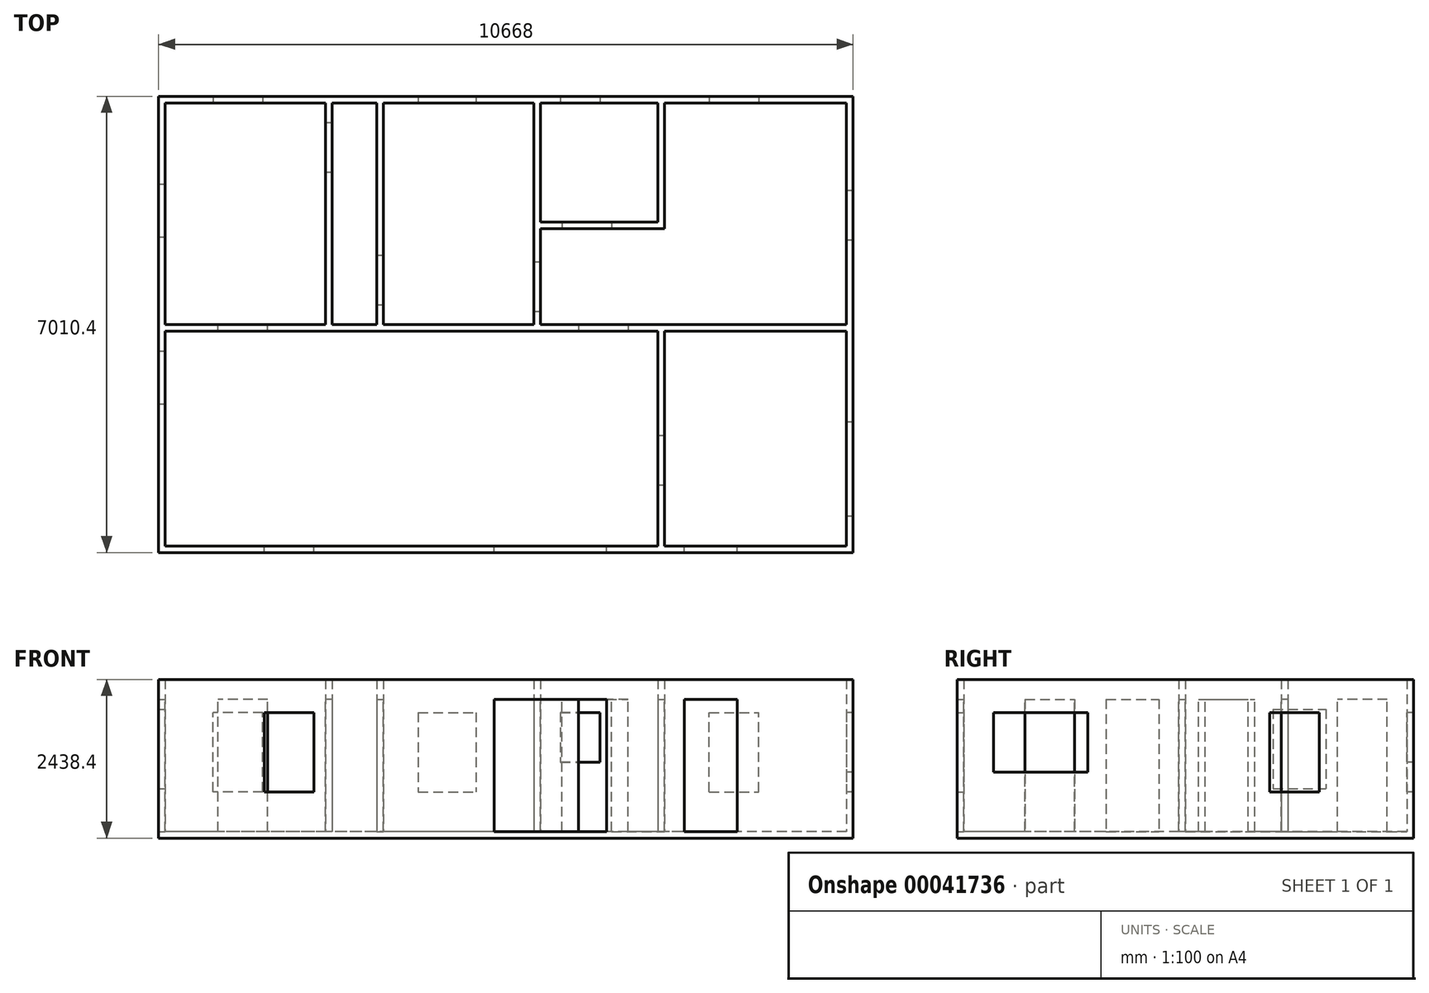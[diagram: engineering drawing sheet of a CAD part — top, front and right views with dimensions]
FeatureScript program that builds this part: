
annotation { "Feature Type Name" : "Feature", "Feature Type Description" : "" }
export const myFeature = defineFeature(function(context is Context, id is Id, definition is map)
    precondition{}
    {
        {
            var Q0;
            Q0=qCreatedBy(makeId("Top.planeOp"),FACE);
            var sketch = newSketch(context, id + "F34", { "sketchPlane" : qUnion([Q0])});
            skLineSegment(sketch, "E0.bottom", {"start": v(10668, 7010.4) * mm, "end": v(0, 7010.4) * mm});
            skLineSegment(sketch, "E0.top", {"start": v(10668, 0) * mm, "end": v(0, 0) * mm});
            skLineSegment(sketch, "E0.left", {"start": v(10668, 7010.4) * mm, "end": v(10668, 0) * mm});
            skLineSegment(sketch, "E0.right", {"start": v(0, 7010.4) * mm, "end": v(0, 0) * mm});
            skSolve(sketch);
        }
        {
            var Q0;
            Q0=qSketchRegion(id+"F34",true);
            extrude(context, id + "F0", {"entities" : qUnion([Q0]), "depth" : 2438.4 * mm});
        }
        {
            var Q0;
            Q0=makeQuery(id+"F0.opExtrude","CAP_FACE",FACE,{"disambiguationData":[OSD([sQuery(id+"F34.wireOp",EDGE,"E0.bottom"),sQuery(id+"F34.wireOp",EDGE,"E0.top"),sQuery(id+"F34.wireOp",EDGE,"E0.left"),sQuery(id+"F34.wireOp",EDGE,"E0.right")])],"isStart":false});
            shell(context, id + "F35", {"entities" : qUnion([Q0]), "thickness" : 101.6 * mm});
        }
        {
            var Q0;
            Q0=makeQuery(id+"F35.opShell","OFFSET_FACE",FACE,{"disambiguationData":[OSD([sQuery(id+"F34.wireOp",EDGE,"E0.bottom"),sQuery(id+"F34.wireOp",EDGE,"E0.top"),sQuery(id+"F34.wireOp",EDGE,"E0.left"),sQuery(id+"F34.wireOp",EDGE,"E0.right")])]});
            var sketch = newSketch(context, id + "F1", { "sketchPlane" : qUnion([Q0])});
            skLineSegment(sketch, "E1", {"start": v(10566.4, 3403.6) * mm, "end": v(101.6, 3403.6) * mm});
            skLineSegment(sketch, "E2.1", {"start": v(10566.4, 3505.2) * mm, "end": v(101.6, 3505.2) * mm});
            skLineSegment(sketch, "E3", {"start": v(3454.4, 6908.8) * mm, "end": v(3454.4, 3505.2) * mm});
            skLineSegment(sketch, "E4", {"start": v(5867.4, 6908.8) * mm, "end": v(5867.4, 3505.2) * mm});
            skLineSegment(sketch, "E5.0", {"start": v(3352.8, 6908.8) * mm, "end": v(3352.8, 3505.2) * mm});
            skLineSegment(sketch, "E6.0", {"start": v(5765.8, 6908.8) * mm, "end": v(5765.8, 3505.2) * mm});
            skLineSegment(sketch, "E7.bottom", {"start": v(2565.4, 3505.2) * mm, "end": v(2667, 3505.2) * mm});
            skLineSegment(sketch, "E7.top", {"start": v(2565.4, 6908.8) * mm, "end": v(2667, 6908.8) * mm});
            skLineSegment(sketch, "E7.left", {"start": v(2565.4, 3505.2) * mm, "end": v(2565.4, 6908.8) * mm});
            skLineSegment(sketch, "E7.right", {"start": v(2667, 3505.2) * mm, "end": v(2667, 6908.8) * mm});
            skLineSegment(sketch, "E8", {"start": v(7670.8, 6908.8) * mm, "end": v(7670.8, 5080) * mm});
            skLineSegment(sketch, "E9", {"start": v(7670.8, 5080) * mm, "end": v(5867.4, 5080) * mm});
            skLineSegment(sketch, "E10", {"start": v(5867.4, 4978.4) * mm, "end": v(7772.4, 4978.4) * mm});
            skLineSegment(sketch, "E11", {"start": v(7772.4, 4978.4) * mm, "end": v(7772.4, 6908.8) * mm});
            skLineSegment(sketch, "E12", {"start": v(7670.8, 3403.6) * mm, "end": v(7670.8, 101.6) * mm});
            skLineSegment(sketch, "E13", {"start": v(7772.4, 3403.6) * mm, "end": v(7772.4, 101.6) * mm});
            skSolve(sketch);
        }
        {
            var Q0;
            Q0=qSketchRegion(id+"F1",true);
            var Q1;
            {var subQ4=sQuery(id+"F1.wireOp",EDGE,"E1");Q1=makeQuery(id+"F1.imprint","IMPRINT",FACE,{"disambiguationData":[TD([[makeQuery(id+"F1.imprint","IMPRINT",EDGE,{"derivedFrom":subQ4}),-1.0]])]});}
            var Q2;
            {var subQ0=sQuery(id+"F1.wireOp",EDGE,"E3");Q2=makeQuery(id+"F1.imprint","IMPRINT",FACE,{"disambiguationData":[TD([[makeQuery(id+"F1.imprint","IMPRINT",EDGE,{"derivedFrom":subQ0}),-1.0]])]});}
            var Q3;
            {var subQ0=sQuery(id+"F1.wireOp",EDGE,"E4");Q3=makeQuery(id+"F1.imprint","IMPRINT",FACE,{"disambiguationData":[TD([[makeQuery(id+"F1.imprint","IMPRINT",EDGE,{"derivedFrom":subQ0}),-1.0]])]});}
            var Q4;
            {var subQ2=sQuery(id+"F1.wireOp",EDGE,"E8");Q4=makeQuery(id+"F1.imprint","IMPRINT",FACE,{"disambiguationData":[TD([[makeQuery(id+"F1.imprint","IMPRINT",EDGE,{"derivedFrom":subQ2}),1.0]])]});}
            var Q5;
            {var subQ0=sQuery(id+"F1.wireOp",EDGE,"E12");Q5=makeQuery(id+"F1.imprint","IMPRINT",FACE,{"disambiguationData":[TD([[makeQuery(id+"F1.imprint","IMPRINT",EDGE,{"derivedFrom":subQ0}),1.0]])]});}
            var Q6;
            Q6=makeQuery(id+"F0.opExtrude","CAP_FACE",FACE,{"disambiguationData":[OSD([sQuery(id+"F34.wireOp",EDGE,"E0.bottom"),sQuery(id+"F34.wireOp",EDGE,"E0.top"),sQuery(id+"F34.wireOp",EDGE,"E0.left"),sQuery(id+"F34.wireOp",EDGE,"E0.right")])],"isStart":false});
            extrude(context, id + "F2", {"entities" : qUnion([Q0, Q1, Q2, Q3, Q4, Q5]), "operationType" : NewBodyOperationType.ADD, "endBound" : BoundingType.UP_TO_SURFACE, "endBoundEntityFace" : qUnion([Q6]), "depth" : 30.48 * mm});
        }
        {
            var Q0;
            {var subQ0=sQuery(id+"F1.wireOp",EDGE,"E2.1");Q0=makeQuery(id+"F2.opExtrude","SWEPT_FACE",FACE,{"disambiguationData":[OSD([subQ0]),TDD([makeQuery(id+"F1.imprint","IMPRINT",EDGE,{"disambiguationData":[TD([[makeQuery(id+"F1.imprint","INTERSECT",VERTEX,{"derivedFrom":[subQ0,sQuery(id+"F1.wireOp",EDGE,"E5.0")]}),-1.0]])],"derivedFrom":subQ0})])]});}
            var sketch = newSketch(context, id + "F36", { "sketchPlane" : qUnion([Q0])});
            skLineSegment(sketch, "E14.bottom", {"start": v(-1676.4, 101.6) * mm, "end": v(-914.4, 101.6) * mm});
            skLineSegment(sketch, "E14.top", {"start": v(-1676.4, 2133.6) * mm, "end": v(-914.4, 2133.6) * mm});
            skLineSegment(sketch, "E14.left", {"start": v(-1676.4, 101.6) * mm, "end": v(-1676.4, 2133.6) * mm});
            skLineSegment(sketch, "E14.right", {"start": v(-914.4, 101.6) * mm, "end": v(-914.4, 2133.6) * mm});
            skSolve(sketch);
        }
        {
            var Q0;
            Q0=qSketchRegion(id+"F36",true);
            extrude(context, id + "F3", {"entities" : qUnion([Q0]), "operationType" : NewBodyOperationType.REMOVE, "endBound" : BoundingType.UP_TO_NEXT, "oppositeDirection" : true, "depth" : 30.48 * mm});
        }
        {
            var Q0;
            Q0=makeQuery(id+"F35.opShell","OFFSET_FACE",FACE,{"disambiguationData":[OSD([sQuery(id+"F34.wireOp",EDGE,"E0.top")])]});
            var sketch = newSketch(context, id + "F37", { "sketchPlane" : qUnion([Q0])});
            skLineSegment(sketch, "E15.bottom", {"start": v(-8890, 101.6) * mm, "end": v(-8077.2, 101.6) * mm});
            skLineSegment(sketch, "E15.top", {"start": v(-8890, 2133.6) * mm, "end": v(-8077.2, 2133.6) * mm});
            skLineSegment(sketch, "E15.left", {"start": v(-8890, 101.6) * mm, "end": v(-8890, 2133.6) * mm});
            skLineSegment(sketch, "E15.right", {"start": v(-8077.2, 101.6) * mm, "end": v(-8077.2, 2133.6) * mm});
            skSolve(sketch);
        }
        {
            var Q0;
            Q0=qSketchRegion(id+"F37",true);
            extrude(context, id + "F38", {"entities" : qUnion([Q0]), "operationType" : NewBodyOperationType.REMOVE, "endBound" : BoundingType.UP_TO_NEXT, "oppositeDirection" : true, "depth" : 30.48 * mm});
        }
        {
            var Q0;
            {var subQ0=sQuery(id+"F34.wireOp",EDGE,"E0.right");var subQ2=sQuery(id+"F34.wireOp",EDGE,"E0.top");Q0=makeQuery(id+"F2.boolean.opBoolean","SPLIT",FACE,{"disambiguationData":[TD([makeQuery(id+"F35.opShell","OFFSET_FACE",FACE,{"disambiguationData":[OSD([subQ2])]})])],"derivedFrom":makeQuery(id+"F35.opShell","OFFSET_FACE",FACE,{"disambiguationData":[OSD([subQ0])]})});}
            var sketch = newSketch(context, id + "F39", { "sketchPlane" : qUnion([Q0])});
            skLineSegment(sketch, "E16.bottom", {"start": v(3098.8, 101.6) * mm, "end": v(2286, 101.6) * mm});
            skLineSegment(sketch, "E16.top", {"start": v(3098.8, 2133.6) * mm, "end": v(2286, 2133.6) * mm});
            skLineSegment(sketch, "E16.left", {"start": v(3098.8, 101.6) * mm, "end": v(3098.8, 2133.6) * mm});
            skLineSegment(sketch, "E16.right", {"start": v(2286, 101.6) * mm, "end": v(2286, 2133.6) * mm});
            skSolve(sketch);
        }
        {
            var Q0;
            Q0=qSketchRegion(id+"F39",true);
            extrude(context, id + "F4", {"entities" : qUnion([Q0]), "operationType" : NewBodyOperationType.REMOVE, "endBound" : BoundingType.UP_TO_NEXT, "oppositeDirection" : true, "depth" : 30.48 * mm});
        }
        {
            var Q0;
            {var subQ0=sQuery(id+"F34.wireOp",EDGE,"E0.right");var subQ3=sQuery(id+"F34.wireOp",EDGE,"E0.bottom");Q0=makeQuery(id+"F2.boolean.opBoolean","SPLIT",FACE,{"disambiguationData":[TD([makeQuery(id+"F35.opShell","OFFSET_FACE",FACE,{"disambiguationData":[OSD([subQ3])]})])],"derivedFrom":makeQuery(id+"F35.opShell","OFFSET_FACE",FACE,{"disambiguationData":[OSD([subQ0])]})});}
            var sketch = newSketch(context, id + "F5", { "sketchPlane" : qUnion([Q0])});
            skLineSegment(sketch, "E17.bottom", {"start": v(4851.4, 1981.2) * mm, "end": v(5664.2, 1981.2) * mm});
            skLineSegment(sketch, "E17.top", {"start": v(4851.4, 762) * mm, "end": v(5664.2, 762) * mm});
            skLineSegment(sketch, "E17.left", {"start": v(4851.4, 1981.2) * mm, "end": v(4851.4, 762) * mm});
            skLineSegment(sketch, "E17.right", {"start": v(5664.2, 1981.2) * mm, "end": v(5664.2, 762) * mm});
            skSolve(sketch);
        }
        {
            var Q0;
            Q0 = qSketchRegion(id + "F5", true);
            extrude(context, id + "F6", {"entities" : qUnion([Q0]), "operationType" : NewBodyOperationType.REMOVE, "endBound" : BoundingType.UP_TO_NEXT, "oppositeDirection" : true, "depth" : 30.48 * mm});
        }
        {
            var Q0;
            Q0=makeQuery(id+"F35.opShell","OFFSET_FACE",FACE,{"disambiguationData":[OSD([sQuery(id+"F34.wireOp",EDGE,"E0.bottom")])]});
            var sketch = newSketch(context, id + "F7", { "sketchPlane" : qUnion([Q0])});
            skLineSegment(sketch, "E18.bottom", {"start": v(838.2, 1930.4) * mm, "end": v(1600.2, 1930.4) * mm});
            skLineSegment(sketch, "E18.top", {"start": v(838.2, 711.2) * mm, "end": v(1600.2, 711.2) * mm});
            skLineSegment(sketch, "E18.left", {"start": v(838.2, 1930.4) * mm, "end": v(838.2, 711.2) * mm});
            skLineSegment(sketch, "E18.right", {"start": v(1600.2, 1930.4) * mm, "end": v(1600.2, 711.2) * mm});
            skSolve(sketch);
        }
        {
            var Q0;
            Q0 = qSketchRegion(id + "F7", true);
            extrude(context, id + "F40", {"entities" : qUnion([Q0]), "operationType" : NewBodyOperationType.REMOVE, "endBound" : BoundingType.UP_TO_NEXT, "oppositeDirection" : true, "depth" : 30.48 * mm});
        }
        {
            var Q0;
            Q0=makeQuery(id+"F2.opExtrude","SWEPT_FACE",FACE,{"disambiguationData":[OSD([sQuery(id+"F1.wireOp",EDGE,"E13")])]});
            var sketch = newSketch(context, id + "F8", { "sketchPlane" : qUnion([Q0])});
            skLineSegment(sketch, "E19.bottom", {"start": v(1041.4, 101.6) * mm, "end": v(1803.4, 101.6) * mm});
            skLineSegment(sketch, "E19.top", {"start": v(1041.4, 2133.6) * mm, "end": v(1803.4, 2133.6) * mm});
            skLineSegment(sketch, "E19.left", {"start": v(1041.4, 101.6) * mm, "end": v(1041.4, 2133.6) * mm});
            skLineSegment(sketch, "E19.right", {"start": v(1803.4, 101.6) * mm, "end": v(1803.4, 2133.6) * mm});
            skSolve(sketch);
        }
        {
            var Q0;
            Q0 = qSketchRegion(id + "F8", true);
            extrude(context, id + "F9", {"entities" : qUnion([Q0]), "operationType" : NewBodyOperationType.REMOVE, "endBound" : BoundingType.UP_TO_NEXT, "oppositeDirection" : true, "depth" : 30.48 * mm});
        }
        {
            var Q0;
            {var subQ0=sQuery(id+"F1.wireOp",EDGE,"E1");Q0=makeQuery(id+"F2.opExtrude","SWEPT_FACE",FACE,{"disambiguationData":[OSD([subQ0]),TDD([makeQuery(id+"F1.imprint","IMPRINT",EDGE,{"disambiguationData":[TD([[makeQuery(id+"F1.imprint","INTERSECT",VERTEX,{"derivedFrom":[subQ0,sQuery(id+"F1.wireOp",EDGE,"E12")]}),-1.0]])],"derivedFrom":subQ0})])]});}
            var sketch = newSketch(context, id + "F10", { "sketchPlane" : qUnion([Q0])});
            skLineSegment(sketch, "E20.bottom", {"start": v(6451.6, 101.6) * mm, "end": v(7213.6, 101.6) * mm});
            skLineSegment(sketch, "E20.top", {"start": v(6451.6, 2133.6) * mm, "end": v(7213.6, 2133.6) * mm});
            skLineSegment(sketch, "E20.left", {"start": v(6451.6, 101.6) * mm, "end": v(6451.6, 2133.6) * mm});
            skLineSegment(sketch, "E20.right", {"start": v(7213.6, 101.6) * mm, "end": v(7213.6, 2133.6) * mm});
            skSolve(sketch);
        }
        {
            var Q0;
            Q0 = qSketchRegion(id + "F10", true);
            extrude(context, id + "F11", {"entities" : qUnion([Q0]), "operationType" : NewBodyOperationType.REMOVE, "endBound" : BoundingType.UP_TO_NEXT, "oppositeDirection" : true, "depth" : 30.48 * mm});
        }
        {
            var Q0;
            Q0=makeQuery(id+"F2.opExtrude","SWEPT_FACE",FACE,{"disambiguationData":[OSD([sQuery(id+"F1.wireOp",EDGE,"E10")])]});
            var sketch = newSketch(context, id + "F12", { "sketchPlane" : qUnion([Q0])});
            skLineSegment(sketch, "E21.bottom", {"start": v(6197.6, 101.6) * mm, "end": v(6959.6, 101.6) * mm});
            skLineSegment(sketch, "E21.top", {"start": v(6197.6, 2133.6) * mm, "end": v(6959.6, 2133.6) * mm});
            skLineSegment(sketch, "E21.left", {"start": v(6197.6, 101.6) * mm, "end": v(6197.6, 2133.6) * mm});
            skLineSegment(sketch, "E21.right", {"start": v(6959.6, 101.6) * mm, "end": v(6959.6, 2133.6) * mm});
            skSolve(sketch);
        }
        {
            var Q0;
            Q0 = qSketchRegion(id + "F12", true);
            extrude(context, id + "F13", {"entities" : qUnion([Q0]), "operationType" : NewBodyOperationType.REMOVE, "endBound" : BoundingType.UP_TO_NEXT, "oppositeDirection" : true, "depth" : 30.48 * mm});
        }
        {
            var Q0;
            {var subQ0=sQuery(id+"F1.wireOp",EDGE,"E4");Q0=makeQuery(id+"F2.opExtrude","SWEPT_FACE",FACE,{"disambiguationData":[OSD([subQ0]),TDD([makeQuery(id+"F1.imprint","IMPRINT",EDGE,{"disambiguationData":[TD([[makeQuery(id+"F1.imprint","INTERSECT",VERTEX,{"derivedFrom":[sQuery(id+"F1.wireOp",EDGE,"E2.1"),subQ0]}),1.0]])],"derivedFrom":subQ0})])]});}
            var sketch = newSketch(context, id + "F14", { "sketchPlane" : qUnion([Q0])});
            skLineSegment(sketch, "E22.bottom", {"start": v(3708.4, 101.6) * mm, "end": v(4470.4, 101.6) * mm});
            skLineSegment(sketch, "E22.top", {"start": v(3708.4, 2133.6) * mm, "end": v(4470.4, 2133.6) * mm});
            skLineSegment(sketch, "E22.left", {"start": v(3708.4, 101.6) * mm, "end": v(3708.4, 2133.6) * mm});
            skLineSegment(sketch, "E22.right", {"start": v(4470.4, 101.6) * mm, "end": v(4470.4, 2133.6) * mm});
            skSolve(sketch);
        }
        {
            var Q0;
            Q0 = qSketchRegion(id + "F14", true);
            extrude(context, id + "F15", {"entities" : qUnion([Q0]), "operationType" : NewBodyOperationType.REMOVE, "endBound" : BoundingType.UP_TO_NEXT, "oppositeDirection" : true, "depth" : 30.48 * mm});
        }
        {
            var Q0;
            {var subQ3=sQuery(id+"F34.wireOp",EDGE,"E0.bottom");Q0=makeQuery(id+"F2.boolean.opBoolean","SPLIT",FACE,{"disambiguationData":[TD([makeQuery(id+"F2.opExtrude","SWEPT_FACE",FACE,{"disambiguationData":[OSD([sQuery(id+"F1.wireOp",EDGE,"E3")])]})])],"derivedFrom":makeQuery(id+"F35.opShell","OFFSET_FACE",FACE,{"disambiguationData":[OSD([subQ3])]})});}
            var sketch = newSketch(context, id + "F16", { "sketchPlane" : qUnion([Q0])});
            skLineSegment(sketch, "E23.bottom", {"start": v(3987.8, 1930.4) * mm, "end": v(4876.8, 1930.4) * mm});
            skLineSegment(sketch, "E23.top", {"start": v(3987.8, 711.2) * mm, "end": v(4876.8, 711.2) * mm});
            skLineSegment(sketch, "E23.left", {"start": v(3987.8, 1930.4) * mm, "end": v(3987.8, 711.2) * mm});
            skLineSegment(sketch, "E23.right", {"start": v(4876.8, 1930.4) * mm, "end": v(4876.8, 711.2) * mm});
            skSolve(sketch);
        }
        {
            var Q0;
            Q0 = qSketchRegion(id + "F16", true);
            extrude(context, id + "F17", {"entities" : qUnion([Q0]), "operationType" : NewBodyOperationType.REMOVE, "endBound" : BoundingType.UP_TO_NEXT, "oppositeDirection" : true, "depth" : 30.48 * mm});
        }
        {
            var Q0;
            {var subQ3=sQuery(id+"F34.wireOp",EDGE,"E0.bottom");Q0=makeQuery(id+"F2.boolean.opBoolean","SPLIT",FACE,{"disambiguationData":[TD([makeQuery(id+"F2.opExtrude","SWEPT_FACE",FACE,{"disambiguationData":[OSD([sQuery(id+"F1.wireOp",EDGE,"E8")])]})])],"derivedFrom":makeQuery(id+"F35.opShell","OFFSET_FACE",FACE,{"disambiguationData":[OSD([subQ3])]})});}
            var sketch = newSketch(context, id + "F18", { "sketchPlane" : qUnion([Q0])});
            skLineSegment(sketch, "E24.bottom", {"start": v(6172.2, 1930.4) * mm, "end": v(6781.8, 1930.4) * mm});
            skLineSegment(sketch, "E24.top", {"start": v(6172.2, 1168.4) * mm, "end": v(6781.8, 1168.4) * mm});
            skLineSegment(sketch, "E24.left", {"start": v(6172.2, 1930.4) * mm, "end": v(6172.2, 1168.4) * mm});
            skLineSegment(sketch, "E24.right", {"start": v(6781.8, 1930.4) * mm, "end": v(6781.8, 1168.4) * mm});
            skSolve(sketch);
        }
        {
            var Q0;
            Q0 = qSketchRegion(id + "F18", true);
            extrude(context, id + "F19", {"entities" : qUnion([Q0]), "operationType" : NewBodyOperationType.REMOVE, "endBound" : BoundingType.UP_TO_NEXT, "oppositeDirection" : true, "depth" : 30.48 * mm});
        }
        {
            var Q0;
            {var subQ1=sQuery(id+"F34.wireOp",EDGE,"E0.left");var subQ2=sQuery(id+"F34.wireOp",EDGE,"E0.top");Q0=makeQuery(id+"F2.boolean.opBoolean","SPLIT",FACE,{"disambiguationData":[TD([makeQuery(id+"F35.opShell","OFFSET_FACE",FACE,{"disambiguationData":[OSD([subQ2])]})])],"derivedFrom":makeQuery(id+"F35.opShell","OFFSET_FACE",FACE,{"disambiguationData":[OSD([subQ1])]})});}
            var sketch = newSketch(context, id + "F20", { "sketchPlane" : qUnion([Q0])});
            skLineSegment(sketch, "E25.bottom", {"start": v(-558.8, 1930.4) * mm, "end": v(-2006.6, 1930.4) * mm});
            skLineSegment(sketch, "E25.top", {"start": v(-558.8, 1016) * mm, "end": v(-2006.6, 1016) * mm});
            skLineSegment(sketch, "E25.left", {"start": v(-558.8, 1930.4) * mm, "end": v(-558.8, 1016) * mm});
            skLineSegment(sketch, "E25.right", {"start": v(-2006.6, 1930.4) * mm, "end": v(-2006.6, 1016) * mm});
            skSolve(sketch);
        }
        {
            var Q0;
            Q0 = qSketchRegion(id + "F20", true);
            extrude(context, id + "F21", {"entities" : qUnion([Q0]), "operationType" : NewBodyOperationType.REMOVE, "endBound" : BoundingType.UP_TO_NEXT, "oppositeDirection" : true, "depth" : 30.48 * mm});
        }
        {
            var Q0;
            {var subQ1=sQuery(id+"F34.wireOp",EDGE,"E0.left");var subQ3=sQuery(id+"F34.wireOp",EDGE,"E0.bottom");Q0=makeQuery(id+"F2.boolean.opBoolean","SPLIT",FACE,{"disambiguationData":[TD([makeQuery(id+"F35.opShell","OFFSET_FACE",FACE,{"disambiguationData":[OSD([subQ1])]})])],"derivedFrom":makeQuery(id+"F35.opShell","OFFSET_FACE",FACE,{"disambiguationData":[OSD([subQ3])]})});}
            var sketch = newSketch(context, id + "F22", { "sketchPlane" : qUnion([Q0])});
            skLineSegment(sketch, "E26.bottom", {"start": v(8458.2, 711.2) * mm, "end": v(9220.2, 711.2) * mm});
            skLineSegment(sketch, "E26.top", {"start": v(8458.2, 1930.4) * mm, "end": v(9220.2, 1930.4) * mm});
            skLineSegment(sketch, "E26.left", {"start": v(8458.2, 711.2) * mm, "end": v(8458.2, 1930.4) * mm});
            skLineSegment(sketch, "E26.right", {"start": v(9220.2, 711.2) * mm, "end": v(9220.2, 1930.4) * mm});
            skSolve(sketch);
        }
        {
            var Q0;
            Q0 = qSketchRegion(id + "F22", true);
            extrude(context, id + "F23", {"entities" : qUnion([Q0]), "operationType" : NewBodyOperationType.REMOVE, "endBound" : BoundingType.UP_TO_NEXT, "oppositeDirection" : true, "depth" : 30.48 * mm});
        }
        {
            var Q0;
            {var subQ1=sQuery(id+"F34.wireOp",EDGE,"E0.left");var subQ3=sQuery(id+"F34.wireOp",EDGE,"E0.bottom");Q0=makeQuery(id+"F2.boolean.opBoolean","SPLIT",FACE,{"disambiguationData":[TD([makeQuery(id+"F35.opShell","OFFSET_FACE",FACE,{"disambiguationData":[OSD([subQ3])]})])],"derivedFrom":makeQuery(id+"F35.opShell","OFFSET_FACE",FACE,{"disambiguationData":[OSD([subQ1])]})});}
            var sketch = newSketch(context, id + "F24", { "sketchPlane" : qUnion([Q0])});
            skLineSegment(sketch, "E27.bottom", {"start": v(-5562.6, 1930.4) * mm, "end": v(-4800.6, 1930.4) * mm});
            skLineSegment(sketch, "E27.top", {"start": v(-5562.6, 711.2) * mm, "end": v(-4800.6, 711.2) * mm});
            skLineSegment(sketch, "E27.left", {"start": v(-5562.6, 1930.4) * mm, "end": v(-5562.6, 711.2) * mm});
            skLineSegment(sketch, "E27.right", {"start": v(-4800.6, 1930.4) * mm, "end": v(-4800.6, 711.2) * mm});
            skSolve(sketch);
        }
        {
            var Q0;
            Q0 = qSketchRegion(id + "F24", true);
            extrude(context, id + "F25", {"entities" : qUnion([Q0]), "operationType" : NewBodyOperationType.REMOVE, "endBound" : BoundingType.UP_TO_NEXT, "oppositeDirection" : true, "depth" : 30.48 * mm});
        }
        {
            var Q0;
            {var subQ0=sQuery(id+"F34.wireOp",EDGE,"E0.right");var subQ2=sQuery(id+"F34.wireOp",EDGE,"E0.top");Q0=makeQuery(id+"F2.boolean.opBoolean","SPLIT",FACE,{"disambiguationData":[TD([makeQuery(id+"F35.opShell","OFFSET_FACE",FACE,{"disambiguationData":[OSD([subQ0])]})])],"derivedFrom":makeQuery(id+"F35.opShell","OFFSET_FACE",FACE,{"disambiguationData":[OSD([subQ2])]})});}
            var sketch = newSketch(context, id + "F26", { "sketchPlane" : qUnion([Q0])});
            skLineSegment(sketch, "E28.bottom", {"start": v(-1625.6, 1930.4) * mm, "end": v(-2387.6, 1930.4) * mm});
            skLineSegment(sketch, "E28.top", {"start": v(-1625.6, 711.2) * mm, "end": v(-2387.6, 711.2) * mm});
            skLineSegment(sketch, "E28.left", {"start": v(-1625.6, 1930.4) * mm, "end": v(-1625.6, 711.2) * mm});
            skLineSegment(sketch, "E28.right", {"start": v(-2387.6, 1930.4) * mm, "end": v(-2387.6, 711.2) * mm});
            skSolve(sketch);
        }
        {
            var Q0;
            Q0 = qSketchRegion(id + "F26", true);
            extrude(context, id + "F27", {"entities" : qUnion([Q0]), "operationType" : NewBodyOperationType.REMOVE, "endBound" : BoundingType.UP_TO_NEXT, "oppositeDirection" : true, "depth" : 30.48 * mm});
        }
        {
            var Q0;
            {var subQ0=sQuery(id+"F34.wireOp",EDGE,"E0.right");var subQ2=sQuery(id+"F34.wireOp",EDGE,"E0.top");Q0=makeQuery(id+"F2.boolean.opBoolean","SPLIT",FACE,{"disambiguationData":[TD([makeQuery(id+"F35.opShell","OFFSET_FACE",FACE,{"disambiguationData":[OSD([subQ0])]})])],"derivedFrom":makeQuery(id+"F35.opShell","OFFSET_FACE",FACE,{"disambiguationData":[OSD([subQ2])]})});}
            var sketch = newSketch(context, id + "F28", { "sketchPlane" : qUnion([Q0])});
            skLineSegment(sketch, "E29.bottom", {"start": v(-5156.2, 101.6) * mm, "end": v(-6883.4, 101.6) * mm});
            skLineSegment(sketch, "E29.top", {"start": v(-5156.2, 2133.6) * mm, "end": v(-6883.4, 2133.6) * mm});
            skLineSegment(sketch, "E29.left", {"start": v(-5156.2, 101.6) * mm, "end": v(-5156.2, 2133.6) * mm});
            skLineSegment(sketch, "E29.right", {"start": v(-6883.4, 101.6) * mm, "end": v(-6883.4, 2133.6) * mm});
            skSolve(sketch);
        }
        {
            var Q0;
            Q0 = qSketchRegion(id + "F28", true);
            extrude(context, id + "F29", {"entities" : qUnion([Q0]), "operationType" : NewBodyOperationType.REMOVE, "endBound" : BoundingType.UP_TO_NEXT, "oppositeDirection" : true, "depth" : 30.48 * mm});
        }
        {
            var Q0;
            Q0=makeQuery(id+"F2.opExtrude","SWEPT_FACE",FACE,{"disambiguationData":[OSD([sQuery(id+"F1.wireOp",EDGE,"E7.left")])]});
            var sketch = newSketch(context, id + "F30", { "sketchPlane" : qUnion([Q0])});
            skLineSegment(sketch, "E30.bottom", {"start": v(-6604, 101.6) * mm, "end": v(-5842, 101.6) * mm});
            skLineSegment(sketch, "E30.top", {"start": v(-6604, 2133.6) * mm, "end": v(-5842, 2133.6) * mm});
            skLineSegment(sketch, "E30.left", {"start": v(-6604, 101.6) * mm, "end": v(-6604, 2133.6) * mm});
            skLineSegment(sketch, "E30.right", {"start": v(-5842, 101.6) * mm, "end": v(-5842, 2133.6) * mm});
            skSolve(sketch);
        }
        {
            var Q0;
            Q0 = qSketchRegion(id + "F30", true);
            extrude(context, id + "F31", {"entities" : qUnion([Q0]), "operationType" : NewBodyOperationType.REMOVE, "endBound" : BoundingType.UP_TO_NEXT, "oppositeDirection" : true, "depth" : 30.48 * mm});
        }
        {
            var Q0;
            Q0=makeQuery(id+"F2.opExtrude","SWEPT_FACE",FACE,{"disambiguationData":[OSD([sQuery(id+"F1.wireOp",EDGE,"E3")])]});
            var sketch = newSketch(context, id + "F32", { "sketchPlane" : qUnion([Q0])});
            skLineSegment(sketch, "E31.bottom", {"start": v(3810, 101.6) * mm, "end": v(4572, 101.6) * mm});
            skLineSegment(sketch, "E31.top", {"start": v(3810, 2133.6) * mm, "end": v(4572, 2133.6) * mm});
            skLineSegment(sketch, "E31.left", {"start": v(3810, 101.6) * mm, "end": v(3810, 2133.6) * mm});
            skLineSegment(sketch, "E31.right", {"start": v(4572, 101.6) * mm, "end": v(4572, 2133.6) * mm});
            skSolve(sketch);
        }
        {
            var Q0;
            Q0 = qSketchRegion(id + "F32", true);
            extrude(context, id + "F33", {"entities" : qUnion([Q0]), "operationType" : NewBodyOperationType.REMOVE, "endBound" : BoundingType.UP_TO_NEXT, "oppositeDirection" : true, "depth" : 30.48 * mm});
        }
    });
